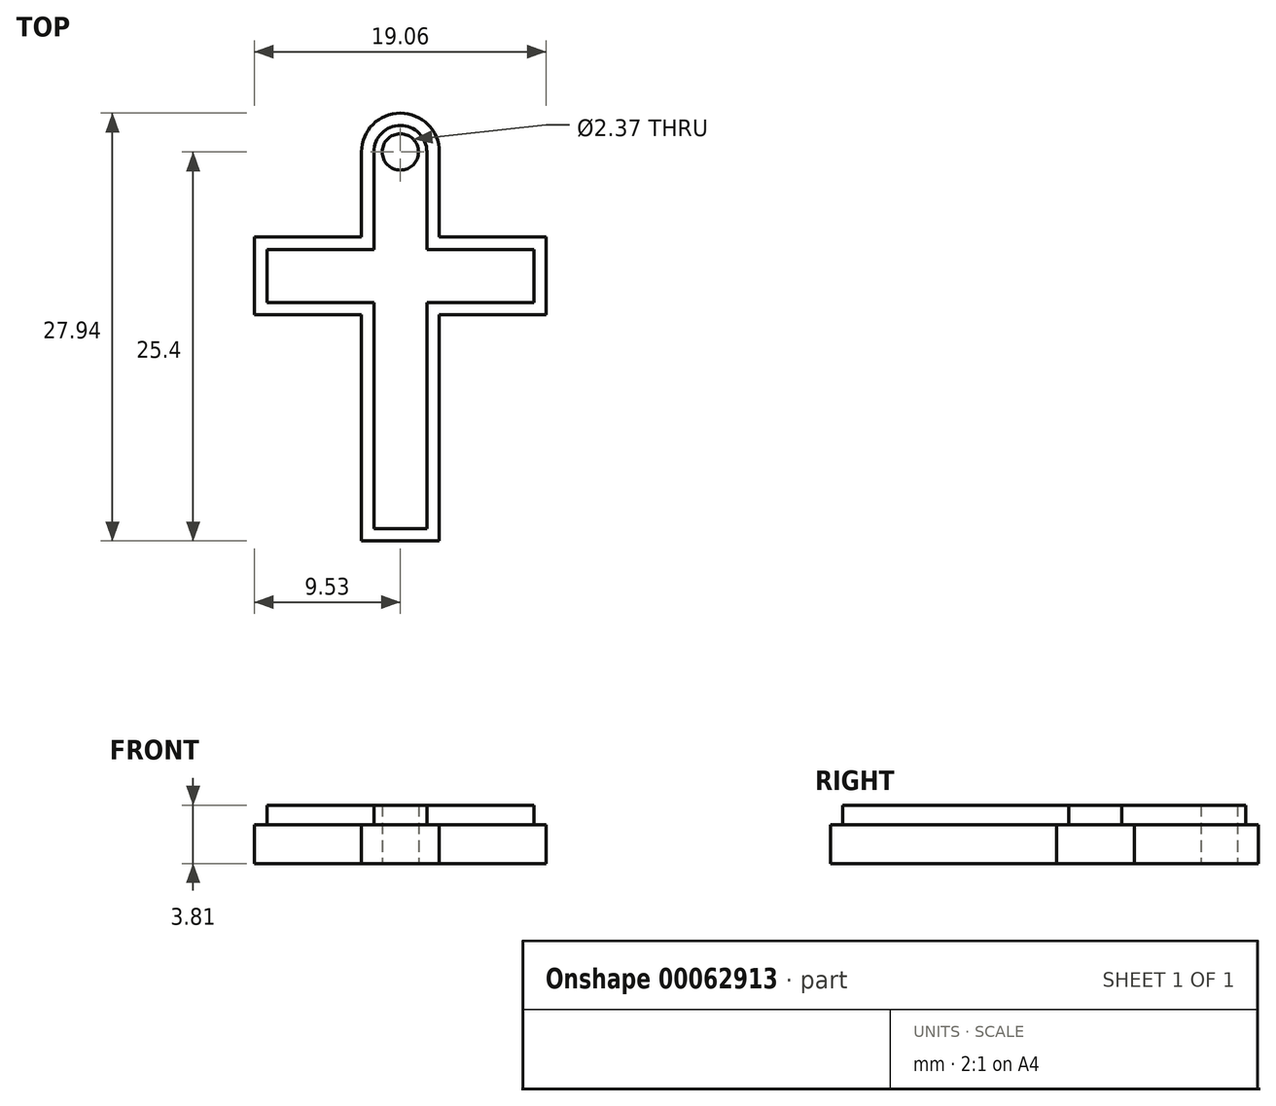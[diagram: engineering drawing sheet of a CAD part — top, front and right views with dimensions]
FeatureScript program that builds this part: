
annotation { "Feature Type Name" : "Feature", "Feature Type Description" : "" }
export const myFeature = defineFeature(function(context is Context, id is Id, definition is map)
    precondition{}
    {
        {
            var Q0;
            Q0=qCreatedBy(makeId("Top.planeOp"),FACE);
            var sketch = newSketch(context, id + "F0", { "sketchPlane" : qUnion([Q0])});
            skLineSegment(sketch, "E0.rect.bottom", {"start": v(-2.54, -12.7) * mm, "end": v(2.54, -12.7) * mm});
            skLineSegment(sketch, "E0.rect.left", {"start": v(-2.54, -12.7) * mm, "end": v(-2.54, 2.07) * mm});
            skLineSegment(sketch, "E0.rect.right", {"start": v(2.54, -12.7) * mm, "end": v(2.54, 2.07) * mm});
            skPoint(sketch, "E0.rect.middle", {"position": v(0, 0) * mm});
            skLineSegment(sketch, "E1.rect.bottom", {"start": v(-9.53, 2.07) * mm, "end": v(-2.54, 2.07) * mm});
            skLineSegment(sketch, "E1.rect.top", {"start": v(-9.53, 7.15) * mm, "end": v(-2.54, 7.15) * mm});
            skLineSegment(sketch, "E1.rect.left", {"start": v(-9.53, 2.07) * mm, "end": v(-9.53, 7.15) * mm});
            skLineSegment(sketch, "E1.rect.right", {"start": v(9.53, 2.07) * mm, "end": v(9.53, 7.15) * mm});
            skPoint(sketch, "E1.rect.middle", {"position": v(0, 4.6) * mm});
            skLineSegment(sketch, "E2.trimOffspring", {"start": v(2.54, 7.15) * mm, "end": v(2.54, 12.7) * mm});
            skLineSegment(sketch, "E3.trimOffspring", {"start": v(2.54, 7.15) * mm, "end": v(9.53, 7.15) * mm});
            skLineSegment(sketch, "E4.trimOffspring", {"start": v(-2.54, 7.15) * mm, "end": v(-2.54, 12.7) * mm});
            skLineSegment(sketch, "E5.trimOffspring", {"start": v(2.54, 2.07) * mm, "end": v(9.53, 2.07) * mm});
            skArc(sketch, "E6", {"start": v(2.54, 12.7) * mm, "mid": v(0, 15.24) * mm, "end": v(-2.54, 12.7) * mm});
            skCircle(sketch, "E7", {"center": v(0, 12.7) * mm, "radius": 1.18 * mm});
            skLineSegment(sketch, "E8.0", {"start": v(1.73, 6.34) * mm, "end": v(1.73, 12.7) * mm});
            skLineSegment(sketch, "E8.1", {"start": v(-1.73, -11.9) * mm, "end": v(1.73, -11.9) * mm});
            skLineSegment(sketch, "E8.2", {"start": v(1.73, -11.9) * mm, "end": v(1.73, 2.88) * mm});
            skLineSegment(sketch, "E8.3", {"start": v(1.73, 2.88) * mm, "end": v(8.72, 2.88) * mm});
            skLineSegment(sketch, "E8.4", {"start": v(8.72, 2.88) * mm, "end": v(8.72, 6.34) * mm});
            skLineSegment(sketch, "E8.5", {"start": v(-1.73, -11.9) * mm, "end": v(-1.73, 2.88) * mm});
            skLineSegment(sketch, "E8.6", {"start": v(1.73, 6.34) * mm, "end": v(8.72, 6.34) * mm});
            skLineSegment(sketch, "E8.7", {"start": v(-8.72, 2.88) * mm, "end": v(-1.73, 2.88) * mm});
            skLineSegment(sketch, "E8.8", {"start": v(-8.72, 2.88) * mm, "end": v(-8.72, 6.34) * mm});
            skLineSegment(sketch, "E8.9", {"start": v(-8.72, 6.34) * mm, "end": v(-1.73, 6.34) * mm});
            skLineSegment(sketch, "E8.10", {"start": v(-1.73, 6.34) * mm, "end": v(-1.73, 12.7) * mm});
            skArc(sketch, "E8.11", {"start": v(1.73, 12.7) * mm, "mid": v(0, 14.43) * mm, "end": v(-1.73, 12.7) * mm});
            skSolve(sketch);
        }
        {
            var Q0;
            Q0=makeQuery(id+"F0.imprint","IMPRINT",FACE,{"disambiguationData":[TD([[makeQuery(id+"F0.imprint","IMPRINT",EDGE,{"derivedFrom":sQuery(id+"F0.wireOp",EDGE,"E0.rect.bottom")}),1.0]])]});
            var Q1;
            Q1=makeQuery(id+"F0.imprint","IMPRINT",FACE,{"disambiguationData":[TD([[makeQuery(id+"F0.imprint","IMPRINT",EDGE,{"derivedFrom":sQuery(id+"F0.wireOp",EDGE,"E7")}),-1.0]])]});
            extrude(context, id + "F1", {"entities" : qUnion([Q0, Q1]), "depth" : 2.54 * mm});
        }
        {
            var Q0;
            Q0=makeQuery(id+"F0.imprint","IMPRINT",FACE,{"disambiguationData":[TD([[makeQuery(id+"F0.imprint","IMPRINT",EDGE,{"derivedFrom":sQuery(id+"F0.wireOp",EDGE,"E7")}),-1.0]])]});
            extrude(context, id + "F2", {"entities" : qUnion([Q0]), "operationType" : NewBodyOperationType.ADD, "depth" : 3.8 * mm});
        }
    });
